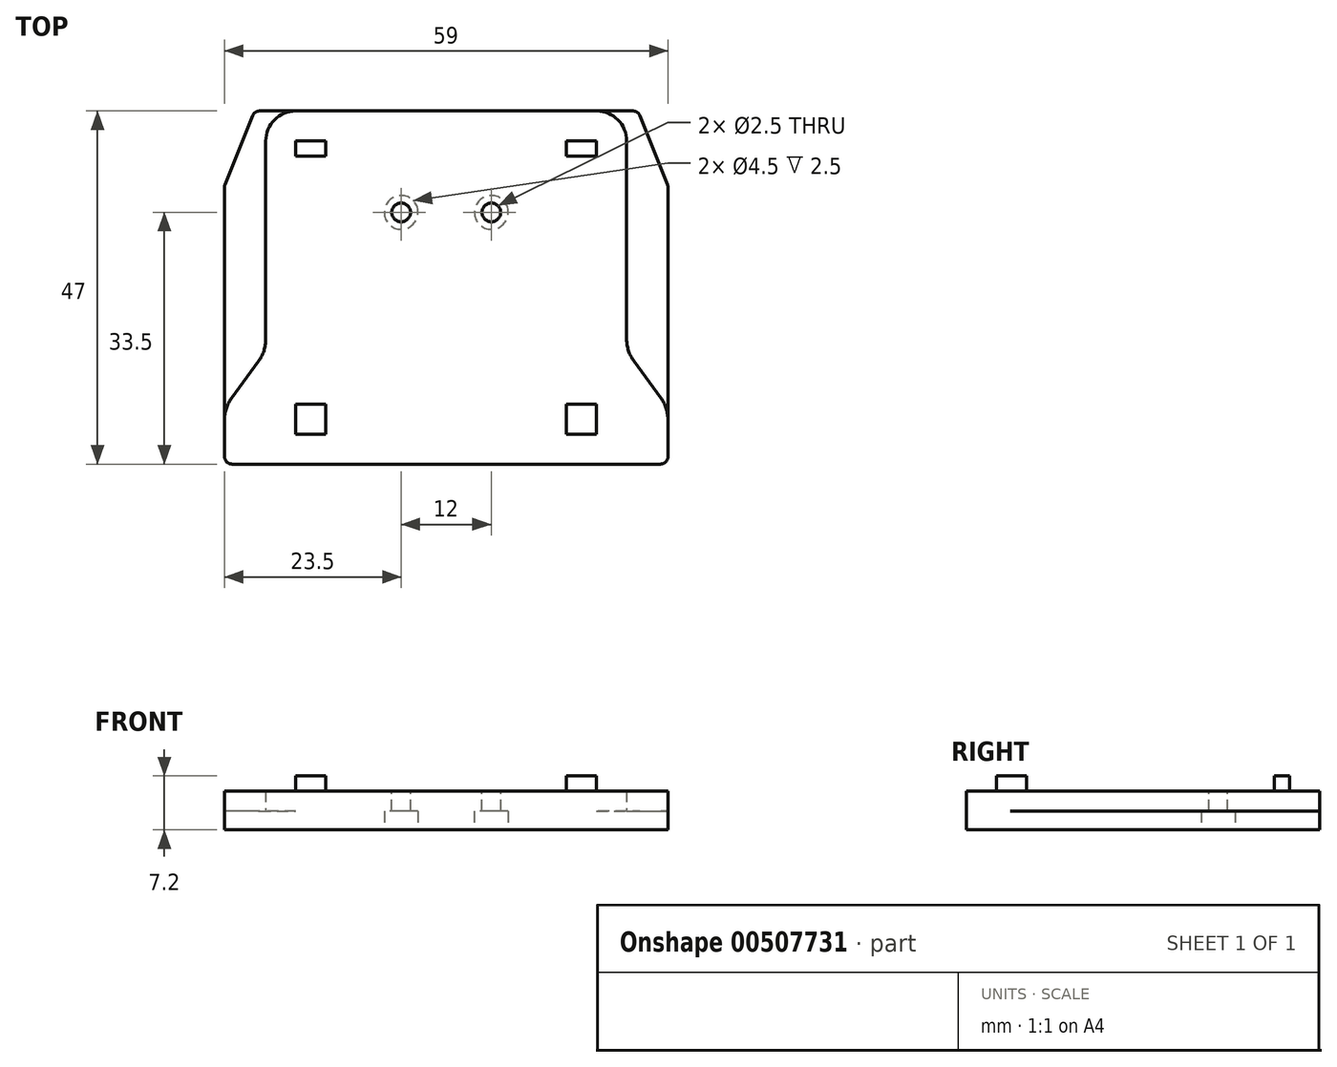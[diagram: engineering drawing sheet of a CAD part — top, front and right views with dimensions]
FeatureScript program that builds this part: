
annotation { "Feature Type Name" : "Feature", "Feature Type Description" : "" }
export const myFeature = defineFeature(function(context is Context, id is Id, definition is map)
    precondition{}
    {
        {
            var Q0;
            Q0=qCreatedBy(makeId("Top.planeOp"),FACE);
            var sketch = newSketch(context, id + "F0", { "sketchPlane" : qUnion([Q0])});
            skLineSegment(sketch, "E0.bottom", {"start": v(4, 0) * mm, "end": v(55, 0) * mm});
            skLineSegment(sketch, "E0.top", {"start": v(0, -47) * mm, "end": v(59, -47) * mm});
            skLineSegment(sketch, "E0.left", {"start": v(0, -10) * mm, "end": v(0, -47) * mm});
            skLineSegment(sketch, "E0.right", {"start": v(59, -10) * mm, "end": v(59, -47) * mm});
            skLineSegment(sketch, "E1", {"start": v(4, 0) * mm, "end": v(0, -10) * mm});
            skPoint(sketch, "E2.orphan", {"position": v(0, 0) * mm});
            skLineSegment(sketch, "E3", {"start": v(55, 0) * mm, "end": v(59, -10) * mm});
            skPoint(sketch, "E4.orphan", {"position": v(59, 0) * mm});
            skSolve(sketch);
        }
        {
            var Q0;
            Q0=makeQuery(id+"F0.imprint","IMPRINT",FACE,{"disambiguationData":[TD([[makeQuery(id+"F0.imprint","IMPRINT",EDGE,{"derivedFrom":sQuery(id+"F0.wireOp",EDGE,"E0.bottom")}),-1.0]])]});
            extrude(context, id + "F1", {"entities" : qUnion([Q0]), "depth" : 2.5 * mm, "offsetDistance" : 25 * mm});
        }
        {
            var Q0;
            Q0=makeQuery(id+"F1.opExtrude","CAP_FACE",FACE,{"disambiguationData":[OSD([sQuery(id+"F0.wireOp",EDGE,"E0.bottom"),sQuery(id+"F0.wireOp",EDGE,"E0.top"),sQuery(id+"F0.wireOp",EDGE,"E0.left"),sQuery(id+"F0.wireOp",EDGE,"E0.right"),sQuery(id+"F0.wireOp",EDGE,"E1"),sQuery(id+"F0.wireOp",EDGE,"E3")])],"isStart":false});
            var sketch = newSketch(context, id + "F2", { "sketchPlane" : qUnion([Q0])});
            skLineSegment(sketch, "E5.bottom", {"start": v(0, -47) * mm, "end": v(59, -47) * mm});
            skLineSegment(sketch, "E5.left", {"start": v(0, -47) * mm, "end": v(0, -39.5) * mm});
            skLineSegment(sketch, "E5.right", {"start": v(59, -47) * mm, "end": v(59, -39.5) * mm});
            skLineSegment(sketch, "E6.top", {"start": v(9.5, 0) * mm, "end": v(49.5, 0) * mm});
            skLineSegment(sketch, "E6.left", {"start": v(5.5, -32) * mm, "end": v(5.5, -4) * mm});
            skLineSegment(sketch, "E6.right", {"start": v(53.5, -32) * mm, "end": v(53.5, -4) * mm});
            skPoint(sketch, "E7.visualSharp", {"position": v(5.5, 0) * mm});
            skArc(sketch, "E7.filletArc", {"start": v(9.5, 0) * mm, "mid": v(6.67, -1.17) * mm, "end": v(5.5, -4) * mm});
            skPoint(sketch, "E8.visualSharp", {"position": v(53.5, 0) * mm});
            skArc(sketch, "E8.filletArc", {"start": v(53.5, -4) * mm, "mid": v(52.33, -1.17) * mm, "end": v(49.5, 0) * mm});
            skLineSegment(sketch, "E9", {"start": v(53.5, -32) * mm, "end": v(59, -39.5) * mm});
            skLineSegment(sketch, "E10", {"start": v(5.5, -32) * mm, "end": v(0, -39.5) * mm});
            skPoint(sketch, "E11.orphan", {"position": v(0, -32) * mm});
            skPoint(sketch, "E12.orphan", {"position": v(59, -32) * mm});
            skSolve(sketch);
        }
        {
            var Q0;
            Q0=makeQuery(id+"F2.imprint","IMPRINT",FACE,{"disambiguationData":[TD([[makeQuery(id+"F2.imprint","IMPRINT",EDGE,{"derivedFrom":sQuery(id+"F2.wireOp",EDGE,"E5.bottom")}),1.0]])]});
            extrude(context, id + "F3", {"entities" : qUnion([Q0]), "operationType" : NewBodyOperationType.ADD, "depth" : 2.7 * mm, "offsetDistance" : 25 * mm});
        }
        {
            var Q0;
            Q0=makeQuery(id+"F3.boolean.opBoolean","MERGE",EDGE,{"derivedFrom":[makeQuery(id+"F1.opExtrude","SWEPT_EDGE",EDGE,{"disambiguationData":[OSD([sQuery(id+"F0.wireOp",EDGE,"E0.top"),sQuery(id+"F0.wireOp",EDGE,"E0.left")])]}),makeQuery(id+"F3.opExtrude","SWEPT_EDGE",EDGE,{"disambiguationData":[OSD([sQuery(id+"F2.wireOp",EDGE,"E5.bottom"),sQuery(id+"F2.wireOp",EDGE,"E5.left")])]})]});
            var Q1;
            Q1=makeQuery(id+"F3.boolean.opBoolean","MERGE",EDGE,{"derivedFrom":[makeQuery(id+"F1.opExtrude","SWEPT_EDGE",EDGE,{"disambiguationData":[OSD([sQuery(id+"F0.wireOp",EDGE,"E0.top"),sQuery(id+"F0.wireOp",EDGE,"E0.right")])]}),makeQuery(id+"F3.opExtrude","SWEPT_EDGE",EDGE,{"disambiguationData":[OSD([sQuery(id+"F2.wireOp",EDGE,"E5.bottom"),sQuery(id+"F2.wireOp",EDGE,"E5.right")])]})]});
            var Q2;
            Q2=makeQuery(id+"F1.opExtrude","SWEPT_EDGE",EDGE,{"disambiguationData":[OSD([sQuery(id+"F0.wireOp",EDGE,"E0.bottom"),sQuery(id+"F0.wireOp",EDGE,"E1")])]});
            var Q3;
            Q3=makeQuery(id+"F1.opExtrude","SWEPT_EDGE",EDGE,{"disambiguationData":[OSD([sQuery(id+"F0.wireOp",EDGE,"E0.bottom"),sQuery(id+"F0.wireOp",EDGE,"E3")])]});
            var Q4;
            Q4=makeQuery(id+"F1.opExtrude","SWEPT_EDGE",EDGE,{"disambiguationData":[OSD([sQuery(id+"F0.wireOp",EDGE,"E0.right"),sQuery(id+"F0.wireOp",EDGE,"E3")])]});
            var Q5;
            Q5=makeQuery(id+"F1.opExtrude","SWEPT_EDGE",EDGE,{"disambiguationData":[OSD([sQuery(id+"F0.wireOp",EDGE,"E0.left"),sQuery(id+"F0.wireOp",EDGE,"E1")])]});
            fillet(context, id + "F4", {"entities" : qUnion([Q0, Q1, Q2, Q3, Q4, Q5]), "radius" : 1 * mm, "tangentPropagation" : true, "allowEdgeOverflow" : false});
        }
        {
            var Q0;
            Q0=makeQuery(id+"F3.opExtrude","SWEPT_EDGE",EDGE,{"disambiguationData":[OSD([sQuery(id+"F0.wireOp",EDGE,"E0.left"),sQuery(id+"F2.wireOp",EDGE,"E5.left"),sQuery(id+"F2.wireOp",EDGE,"E10")])]});
            var Q1;
            Q1=makeQuery(id+"F3.opExtrude","SWEPT_EDGE",EDGE,{"disambiguationData":[OSD([sQuery(id+"F0.wireOp",EDGE,"E0.right"),sQuery(id+"F2.wireOp",EDGE,"E5.right"),sQuery(id+"F2.wireOp",EDGE,"E9")])]});
            var Q2;
            Q2=makeQuery(id+"F3.opExtrude","SWEPT_EDGE",EDGE,{"disambiguationData":[OSD([sQuery(id+"F2.wireOp",EDGE,"E6.right"),sQuery(id+"F2.wireOp",EDGE,"E9")])]});
            var Q3;
            Q3=makeQuery(id+"F3.opExtrude","SWEPT_EDGE",EDGE,{"disambiguationData":[OSD([sQuery(id+"F2.wireOp",EDGE,"E6.left"),sQuery(id+"F2.wireOp",EDGE,"E10")])]});
            fillet(context, id + "F5", {"entities" : qUnion([Q0, Q1, Q2, Q3]), "radius" : 5 * mm, "tangentPropagation" : true, "allowEdgeOverflow" : false});
        }
        {
            var Q0;
            Q0=makeQuery(id+"F3.opExtrude","CAP_FACE",FACE,{"disambiguationData":[OSD([sQuery(id+"F2.wireOp",EDGE,"E5.bottom"),sQuery(id+"F2.wireOp",EDGE,"E5.left"),sQuery(id+"F2.wireOp",EDGE,"E5.right"),sQuery(id+"F2.wireOp",EDGE,"E6.top"),sQuery(id+"F2.wireOp",EDGE,"E6.left"),sQuery(id+"F2.wireOp",EDGE,"E6.right"),sQuery(id+"F2.wireOp",EDGE,"E7.filletArc"),sQuery(id+"F2.wireOp",EDGE,"E8.filletArc"),sQuery(id+"F2.wireOp",EDGE,"E9"),sQuery(id+"F2.wireOp",EDGE,"E10")])],"isStart":false});
            var sketch = newSketch(context, id + "F6", { "sketchPlane" : qUnion([Q0])});
            skLineSegment(sketch, "E13.bottom", {"start": v(9.5, -4) * mm, "end": v(13.5, -4) * mm});
            skLineSegment(sketch, "E13.top", {"start": v(9.5, -6) * mm, "end": v(13.5, -6) * mm});
            skLineSegment(sketch, "E13.left", {"start": v(9.5, -4) * mm, "end": v(9.5, -6) * mm});
            skLineSegment(sketch, "E13.right", {"start": v(13.5, -4) * mm, "end": v(13.5, -6) * mm});
            skLineSegment(sketch, "E14.bottom", {"start": v(9.5, -39) * mm, "end": v(13.5, -39) * mm});
            skLineSegment(sketch, "E14.top", {"start": v(9.5, -43) * mm, "end": v(13.5, -43) * mm});
            skLineSegment(sketch, "E14.left", {"start": v(9.5, -39) * mm, "end": v(9.5, -43) * mm});
            skLineSegment(sketch, "E14.right", {"start": v(13.5, -39) * mm, "end": v(13.5, -43) * mm});
            skLineSegment(sketch, "E15.bottom", {"start": v(45.5, -4) * mm, "end": v(49.5, -4) * mm});
            skLineSegment(sketch, "E15.top", {"start": v(45.5, -6) * mm, "end": v(49.5, -6) * mm});
            skLineSegment(sketch, "E15.left", {"start": v(45.5, -4) * mm, "end": v(45.5, -6) * mm});
            skLineSegment(sketch, "E15.right", {"start": v(49.5, -4) * mm, "end": v(49.5, -6) * mm});
            skLineSegment(sketch, "E16.bottom", {"start": v(45.5, -39) * mm, "end": v(49.5, -39) * mm});
            skLineSegment(sketch, "E16.top", {"start": v(45.5, -43) * mm, "end": v(49.5, -43) * mm});
            skLineSegment(sketch, "E16.left", {"start": v(45.5, -39) * mm, "end": v(45.5, -43) * mm});
            skLineSegment(sketch, "E16.right", {"start": v(49.5, -39) * mm, "end": v(49.5, -43) * mm});
            skSolve(sketch);
        }
        {
            var Q0;
            Q0 = qSketchRegion(id + "F6", true);
            extrude(context, id + "F7", {"entities" : qUnion([Q0]), "operationType" : NewBodyOperationType.ADD, "depth" : 2 * mm, "offsetDistance" : 25 * mm});
        }
        {
            var Q0;
            Q0=makeQuery(id+"F6.imprint","IMPRINT",FACE,{"disambiguationData":[TD([[makeQuery(id+"F6.imprint","IMPRINT",EDGE,{"derivedFrom":sQuery(id+"F6.wireOp",EDGE,"E13.bottom")}),1.0]])]});
            var sketch = newSketch(context, id + "F8", { "sketchPlane" : qUnion([Q0])});
            skCircle(sketch, "E17", {"center": v(23.5, -13.5) * mm, "radius": 1.25 * mm});
            skCircle(sketch, "E18", {"center": v(35.5, -13.5) * mm, "radius": 1.25 * mm});
            skSolve(sketch);
        }
        {
            var Q0;
            Q0 = qSketchRegion(id + "F8", true);
            extrude(context, id + "F9", {"entities" : qUnion([Q0]), "operationType" : NewBodyOperationType.REMOVE, "oppositeDirection" : true, "depth" : 6 * mm, "offsetDistance" : 25 * mm});
        }
        {
            var Q0;
            Q0=makeQuery(id+"F0.imprint","IMPRINT",FACE,{"disambiguationData":[TD([[makeQuery(id+"F0.imprint","IMPRINT",EDGE,{"derivedFrom":sQuery(id+"F0.wireOp",EDGE,"E0.bottom")}),-1.0]])]});
            var sketch = newSketch(context, id + "F10", { "sketchPlane" : qUnion([Q0])});
            skCircle(sketch, "E19", {"center": v(35.5, -13.5) * mm, "radius": 2.25 * mm});
            skCircle(sketch, "E20", {"center": v(23.5, -13.5) * mm, "radius": 2.25 * mm});
            skSolve(sketch);
        }
        {
            var Q0;
            Q0 = qSketchRegion(id + "F10", true);
            extrude(context, id + "F11", {"entities" : qUnion([Q0]), "operationType" : NewBodyOperationType.REMOVE, "depth" : 2.5 * mm, "offsetDistance" : 25 * mm});
        }
    });
